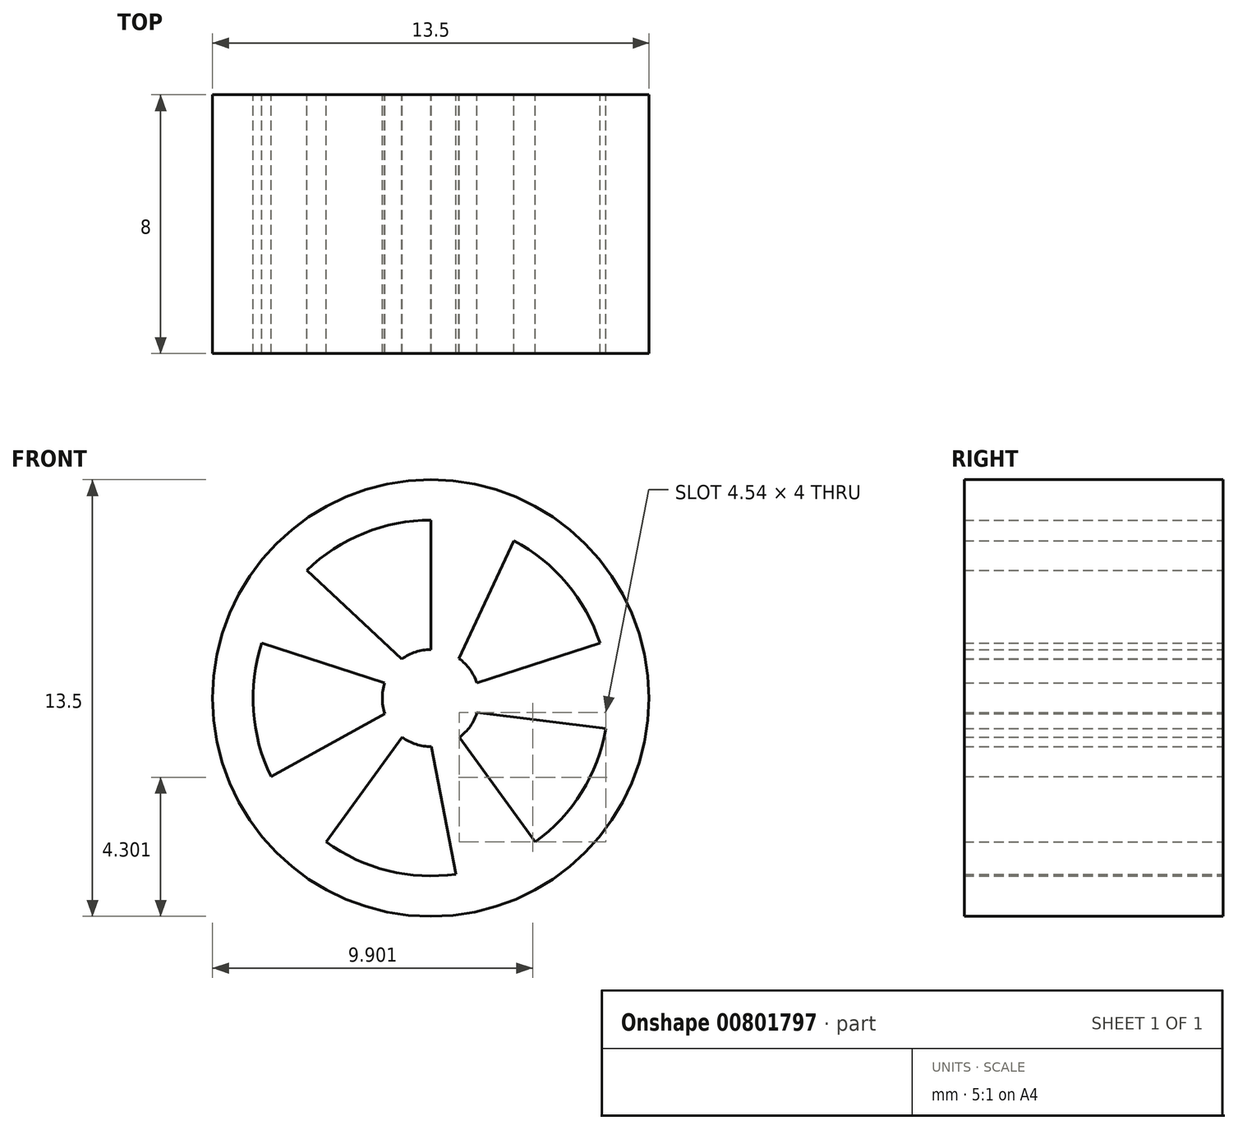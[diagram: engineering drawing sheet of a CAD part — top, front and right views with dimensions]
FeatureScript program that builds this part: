
annotation { "Feature Type Name" : "Feature", "Feature Type Description" : "" }
export const myFeature = defineFeature(function(context is Context, id is Id, definition is map)
    precondition{}
    {
        {
            var Q0;
            Q0=qCreatedBy(makeId("Front.planeOp"),FACE);
            var sketch = newSketch(context, id + "F0", { "sketchPlane" : qUnion([Q0])});
            skCircle(sketch, "E0", {"center": v(0, 0) * mm, "radius": 6.75 * mm});
            skSolve(sketch);
        }
        {
            var Q0;
            Q0=makeQuery(id+"F0.imprint","IMPRINT",FACE,{"disambiguationData":[TD([[makeQuery(id+"F0.imprint","IMPRINT",EDGE,{"derivedFrom":sQuery(id+"F0.wireOp",EDGE,"E0")}),1.0]])]});
            extrude(context, id + "F1", {"entities" : qUnion([Q0]), "depth" : 8 * mm, "offsetDistance" : 25 * mm});
        }
        {
            var Q0;
            Q0=qCreatedBy(makeId("Front.planeOp"),FACE);
            var sketch = newSketch(context, id + "F2", { "sketchPlane" : qUnion([Q0])});
            skCircle(sketch, "E1", {"center": v(0, 0) * mm, "radius": 5.5 * mm});
            skArc(sketch, "E2", {"start": v(0, 1.5) * mm, "mid": v(-0.46, -1.43) * mm, "end": v(0.87, 1.22) * mm});
            skLineSegment(sketch, "E3", {"start": v(0, 1.5) * mm, "end": v(0, 5.5) * mm});
            skLineSegment(sketch, "E4", {"start": v(2.57, 4.86) * mm, "end": v(0.87, 1.22) * mm});
            skLineSegment(sketch, "E5.1.0", {"start": v(-1.43, 0.46) * mm, "end": v(-5.23, 1.7) * mm});
            skLineSegment(sketch, "E5.1.1", {"start": v(-3.83, 3.94) * mm, "end": v(-0.9, 1.2) * mm});
            skLineSegment(sketch, "E5.2.0", {"start": v(-0.88, -1.21) * mm, "end": v(-3.23, -4.45) * mm});
            skLineSegment(sketch, "E5.2.1", {"start": v(-4.94, -2.43) * mm, "end": v(-1.42, -0.48) * mm});
            skLineSegment(sketch, "E5.3.0", {"start": v(0.88, -1.21) * mm, "end": v(3.23, -4.45) * mm});
            skLineSegment(sketch, "E5.3.1", {"start": v(0.78, -5.44) * mm, "end": v(0.02, -1.5) * mm});
            skLineSegment(sketch, "E5.4.0", {"start": v(1.43, 0.46) * mm, "end": v(5.23, 1.7) * mm});
            skLineSegment(sketch, "E5.4.1", {"start": v(5.42, -0.94) * mm, "end": v(1.43, -0.45) * mm});
            skSolve(sketch);
        }
        {
            var Q0;
            {var subQ0=sQuery(id+"F2.wireOp",EDGE,"E3");Q0=makeQuery(id+"F2.imprint","IMPRINT",FACE,{"disambiguationData":[TD([[makeQuery(id+"F2.imprint","IMPRINT",EDGE,{"derivedFrom":subQ0}),1.0]])]});}
            var Q1;
            {var subQ0=sQuery(id+"F2.wireOp",EDGE,"E4");Q1=makeQuery(id+"F2.imprint","IMPRINT",FACE,{"disambiguationData":[TD([[makeQuery(id+"F2.imprint","IMPRINT",EDGE,{"derivedFrom":subQ0}),1.0]])]});}
            var Q2;
            {var subQ0=sQuery(id+"F2.wireOp",EDGE,"E5.3.0");Q2=makeQuery(id+"F2.imprint","IMPRINT",FACE,{"disambiguationData":[TD([[makeQuery(id+"F2.imprint","IMPRINT",EDGE,{"derivedFrom":subQ0}),1.0]])]});}
            var Q3;
            {var subQ0=sQuery(id+"F2.wireOp",EDGE,"E5.1.0");Q3=makeQuery(id+"F2.imprint","IMPRINT",FACE,{"disambiguationData":[TD([[makeQuery(id+"F2.imprint","IMPRINT",EDGE,{"derivedFrom":subQ0}),1.0]])]});}
            var Q4;
            {var subQ0=sQuery(id+"F2.wireOp",EDGE,"E5.2.0");Q4=makeQuery(id+"F2.imprint","IMPRINT",FACE,{"disambiguationData":[TD([[makeQuery(id+"F2.imprint","IMPRINT",EDGE,{"derivedFrom":subQ0}),1.0]])]});}
            extrude(context, id + "F3", {"entities" : qUnion([Q0, Q1, Q2, Q3, Q4]), "operationType" : NewBodyOperationType.REMOVE, "endBound" : BoundingType.THROUGH_ALL, "depth" : 25 * mm, "offsetDistance" : 25 * mm});
        }
    });
